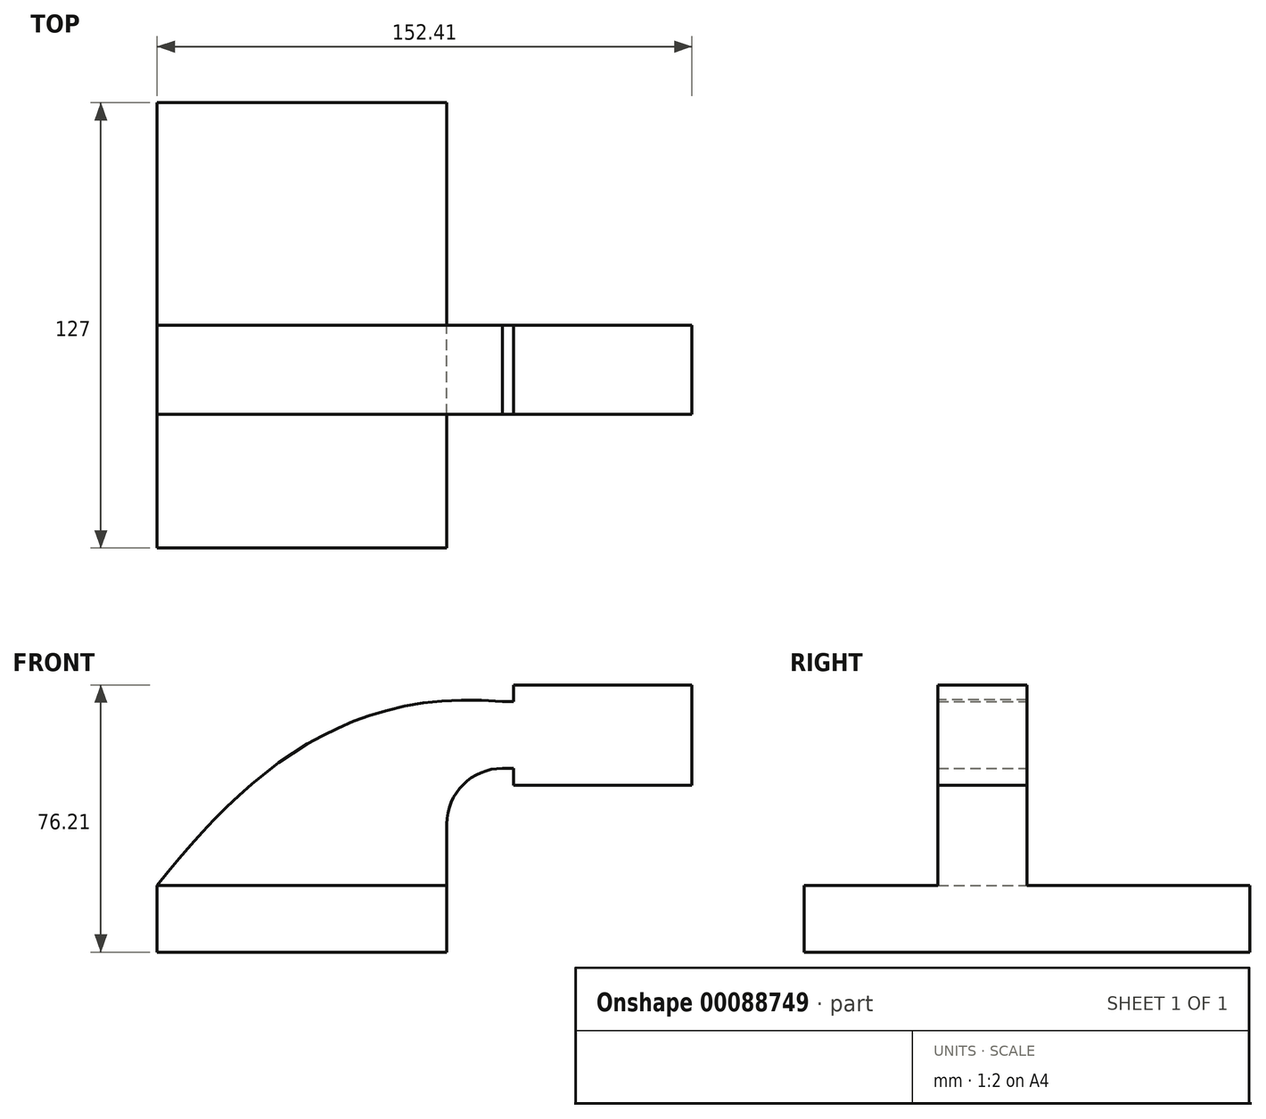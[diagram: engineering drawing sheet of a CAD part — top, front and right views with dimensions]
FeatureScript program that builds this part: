
annotation { "Feature Type Name" : "Feature", "Feature Type Description" : "" }
export const myFeature = defineFeature(function(context is Context, id is Id, definition is map)
    precondition{}
    {
        {
            var Q0;
            Q0=qCreatedBy(makeId("Front.planeOp"),FACE);
            var sketch = newSketch(context, id + "F0", { "sketchPlane" : qUnion([Q0])});
            skLineSegment(sketch, "E0.bottom", {"start": v(-41.28, 9.52) * mm, "end": v(41.28, 9.53) * mm});
            skLineSegment(sketch, "E0.top", {"start": v(-41.28, -9.52) * mm, "end": v(41.28, -9.52) * mm});
            skLineSegment(sketch, "E0.left", {"start": v(-41.28, 9.52) * mm, "end": v(-41.27, -9.53) * mm});
            skLineSegment(sketch, "E0.right", {"start": v(41.28, 9.53) * mm, "end": v(41.28, -9.52) * mm});
            skPoint(sketch, "E0.middle", {"position": v(0, 0) * mm});
            skLineSegment(sketch, "E1.bottom", {"start": v(60.33, 38.1) * mm, "end": v(111.12, 38.1) * mm});
            skLineSegment(sketch, "E1.top", {"start": v(60.32, 66.67) * mm, "end": v(111.12, 66.67) * mm});
            skLineSegment(sketch, "E1.left", {"start": v(60.32, 38.1) * mm, "end": v(60.32, 66.68) * mm});
            skLineSegment(sketch, "E1.right", {"start": v(111.12, 38.1) * mm, "end": v(111.12, 66.68) * mm});
            skPoint(sketch, "E1.middle", {"position": v(85.72, 52.39) * mm});
            skLineSegment(sketch, "E2", {"start": v(41.27, 9.53) * mm, "end": v(41.27, 27) * mm});
            skArc(sketch, "E3", {"start": v(41.27, 27) * mm, "mid": v(45.92, 38.23) * mm, "end": v(57.15, 42.88) * mm});
            skLineSegment(sketch, "E4", {"start": v(57.15, 42.88) * mm, "end": v(85.72, 42.88) * mm});
            skLineSegment(sketch, "E5.0", {"start": v(57.15, 61.93) * mm, "end": v(85.72, 61.93) * mm});
            skArc(sketch, "E5.1", {"start": v(22.23, 27) * mm, "mid": v(32.45, 51.7) * mm, "end": v(57.15, 61.93) * mm});
            skLineSegment(sketch, "E5.2", {"start": v(22.22, 9.53) * mm, "end": v(22.22, 27) * mm});
            skLineSegment(sketch, "E6", {"start": v(85.72, 38.1) * mm, "end": v(85.72, 66.67) * mm});
            skPoint(sketch, "E7.orphan", {"position": v(99.2, 42.88) * mm});
            skFitSpline(sketch, "E8", {"points": [v(-41.28, 9.52) * mm, v(57.15, 61.93) * mm], "startDerivative": vector(71.25, 89.71) * mm, "endDerivative": vector(139.12, -12.84) * mm});
            skSolve(sketch);
        }
        {
            var Q0;
            Q0=makeQuery(id+"F0.imprint","IMPRINT",FACE,{"disambiguationData":[TD([[makeQuery(id+"F0.imprint","IMPRINT",EDGE,{"derivedFrom":sQuery(id+"F0.wireOp",EDGE,"E0.top")}),1.0]])]});
            extrude(context, id + "F1", {"entities" : qUnion([Q0]), "endBound" : BoundingType.SYMMETRIC, "depth" : 127 * mm});
        }
        {
            var Q0;
            Q0 = qSketchRegion(id + "F0", true);
            extrude(context, id + "F2", {"entities" : qUnion([Q0]), "operationType" : NewBodyOperationType.ADD, "depth" : 25.4 * mm});
        }
    });
